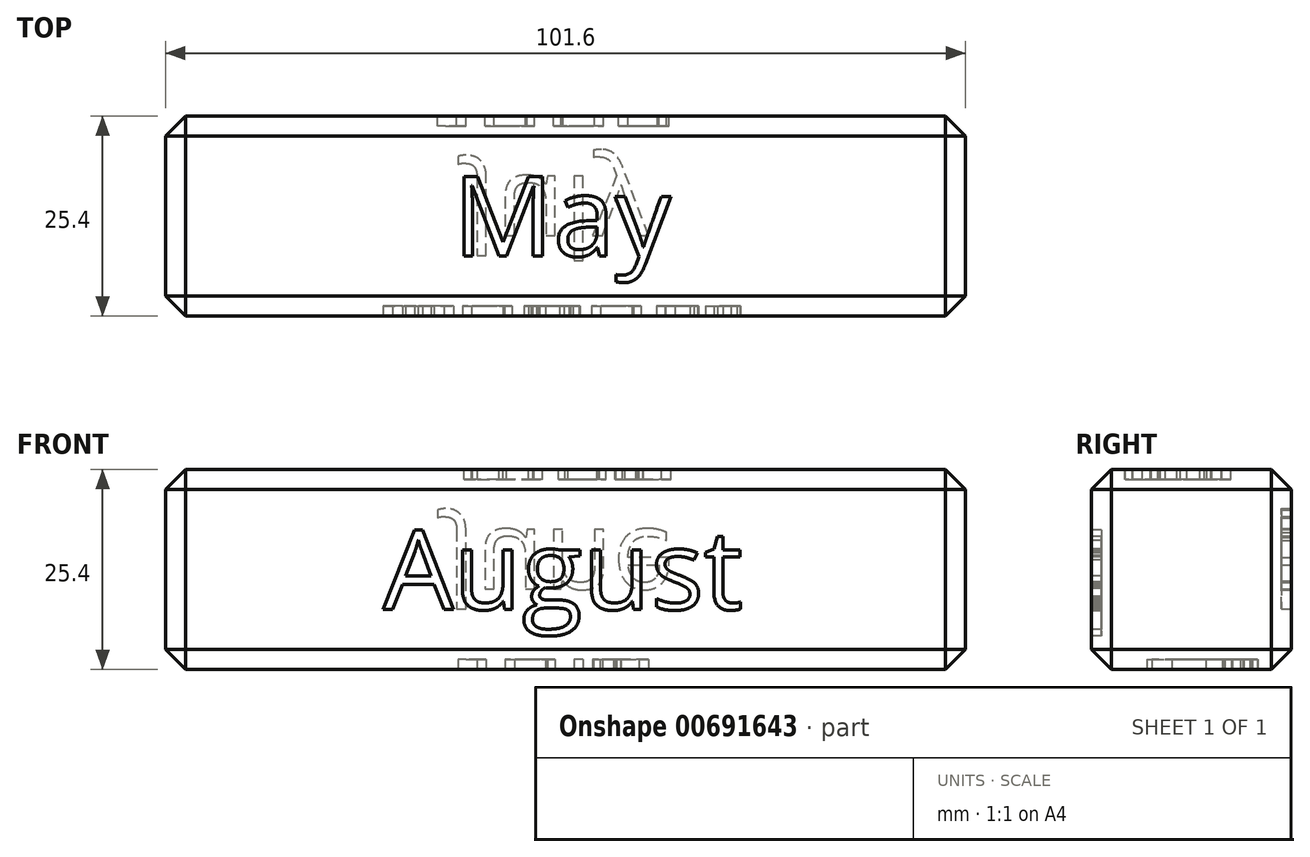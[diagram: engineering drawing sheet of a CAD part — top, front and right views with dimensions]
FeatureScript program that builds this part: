
annotation { "Feature Type Name" : "Feature", "Feature Type Description" : "" }
export const myFeature = defineFeature(function(context is Context, id is Id, definition is map)
    precondition{}
    {
        {
            var Q0;
            Q0=qCreatedBy(makeId("Top.planeOp"),FACE);
            var sketch = newSketch(context, id + "F0", { "sketchPlane" : qUnion([Q0])});
            skLineSegment(sketch, "E0.bottom", {"start": v(50.8, 12.7) * mm, "end": v(-50.8, 12.7) * mm});
            skLineSegment(sketch, "E0.top", {"start": v(50.8, -12.7) * mm, "end": v(-50.8, -12.7) * mm});
            skLineSegment(sketch, "E0.left", {"start": v(50.8, 12.7) * mm, "end": v(50.8, -12.7) * mm});
            skLineSegment(sketch, "E0.right", {"start": v(-50.8, 12.7) * mm, "end": v(-50.8, -12.7) * mm});
            skPoint(sketch, "E0.middle", {"position": v(0, 0) * mm});
            skSolve(sketch);
        }
        {
            var Q0;
            Q0 = qSketchRegion(id + "F0", true);
            extrude(context, id + "F1", {"entities" : qUnion([Q0]), "depth" : 12.7 * mm, "offsetDistance" : 25.4 * mm, "hasSecondDirection" : true, "secondDirectionOppositeDirection" : true, "secondDirectionDepth" : 12.7 * mm});
        }
        {
            var Q0;
            Q0=makeQuery(id+"F1.opExtrude","CAP_FACE",FACE,{"disambiguationData":[OSD([sQuery(id+"F0.wireOp",EDGE,"E0.bottom"),sQuery(id+"F0.wireOp",EDGE,"E0.top"),sQuery(id+"F0.wireOp",EDGE,"E0.left"),sQuery(id+"F0.wireOp",EDGE,"E0.right")])],"isStart":false});
            var Q1;
            Q1=makeQuery(id+"F1.opExtrude","SWEPT_FACE",FACE,{"disambiguationData":[OSD([sQuery(id+"F0.wireOp",EDGE,"E0.top")])]});
            var Q2;
            Q2=makeQuery(id+"F1.opExtrude","SWEPT_FACE",FACE,{"disambiguationData":[OSD([sQuery(id+"F0.wireOp",EDGE,"E0.right")])]});
            var Q3;
            Q3=makeQuery(id+"F1.opExtrude","CAP_FACE",FACE,{"disambiguationData":[OSD([sQuery(id+"F0.wireOp",EDGE,"E0.bottom"),sQuery(id+"F0.wireOp",EDGE,"E0.top"),sQuery(id+"F0.wireOp",EDGE,"E0.left"),sQuery(id+"F0.wireOp",EDGE,"E0.right")])],"isStart":true});
            var Q4;
            Q4=makeQuery(id+"F1.opExtrude","SWEPT_FACE",FACE,{"disambiguationData":[OSD([sQuery(id+"F0.wireOp",EDGE,"E0.bottom")])]});
            chamfer(context, id + "F2", {"entities" : qUnion([Q0, Q1, Q2, Q3, Q4]), "width" : 2.54 * mm, "tangentPropagation" : true});
        }
        {
            var Q0;
            Q0=makeQuery(id+"F1.opExtrude","CAP_FACE",FACE,{"disambiguationData":[OSD([sQuery(id+"F0.wireOp",EDGE,"E0.bottom"),sQuery(id+"F0.wireOp",EDGE,"E0.top"),sQuery(id+"F0.wireOp",EDGE,"E0.left"),sQuery(id+"F0.wireOp",EDGE,"E0.right")])],"isStart":false});
            var sketch = newSketch(context, id + "F3", { "sketchPlane" : qUnion([Q0])});
            skText(sketch, "E1", { "text": "May", "fontName": "OpenSans-Regular.ttf"});
            skLineSegment(sketch, "E2", {"start": v(-14.3, 0) * mm, "end": v(-61.84, 0) * mm, "construction": true});
            const initialGuessF3  = {"E1": [-0.0143, -0.00508, 1, 0, 0.01016]};
            skSetInitialGuess(sketch, initialGuessF3);
            skSolve(sketch);
        }
        {
            var Q0;
            Q0 = qSketchRegion(id + "F3", true);
            extrude(context, id + "F4", {"entities" : qUnion([Q0]), "operationType" : NewBodyOperationType.REMOVE, "oppositeDirection" : true, "depth" : 1.27 * mm, "offsetDistance" : 25.4 * mm});
        }
        {
            var Q0;
            Q0=makeQuery(id+"F1.opExtrude","SWEPT_FACE",FACE,{"disambiguationData":[OSD([sQuery(id+"F0.wireOp",EDGE,"E0.bottom")])]});
            var sketch = newSketch(context, id + "F5", { "sketchPlane" : qUnion([Q0])});
            skText(sketch, "E3", { "text": "June", "fontName": "OpenSans-Regular.ttf"});
            skLineSegment(sketch, "E4", {"start": v(58.9, 0) * mm, "end": v(15.14, 0) * mm, "construction": true});
            const initialGuessF5  = {"E3": [0.01514, 0.00508, -1, 0, 0.01016]};
            skSetInitialGuess(sketch, initialGuessF5);
            skSolve(sketch);
        }
        {
            var Q0;
            Q0 = qSketchRegion(id + "F5", true);
            extrude(context, id + "F6", {"entities" : qUnion([Q0]), "operationType" : NewBodyOperationType.REMOVE, "oppositeDirection" : true, "depth" : 1.27 * mm, "offsetDistance" : 25.4 * mm});
        }
        {
            var Q0;
            Q0=makeQuery(id+"F1.opExtrude","CAP_FACE",FACE,{"disambiguationData":[OSD([sQuery(id+"F0.wireOp",EDGE,"E0.bottom"),sQuery(id+"F0.wireOp",EDGE,"E0.top"),sQuery(id+"F0.wireOp",EDGE,"E0.left"),sQuery(id+"F0.wireOp",EDGE,"E0.right")])],"isStart":true});
            var sketch = newSketch(context, id + "F7", { "sketchPlane" : qUnion([Q0])});
            skText(sketch, "E5", { "text": "July", "fontName": "OpenSans-Regular.ttf"});
            skLineSegment(sketch, "E6", {"start": v(-57.55, 0) * mm, "end": v(-12.56, 0) * mm, "construction": true});
            const initialGuessF7  = {"E5": [-0.01256, -0.00508, 1, 0, 0.01016]};
            skSetInitialGuess(sketch, initialGuessF7);
            skSolve(sketch);
        }
        {
            var Q0;
            Q0 = qSketchRegion(id + "F7", true);
            extrude(context, id + "F8", {"entities" : qUnion([Q0]), "operationType" : NewBodyOperationType.REMOVE, "oppositeDirection" : true, "depth" : 1.27 * mm, "offsetDistance" : 25.4 * mm});
        }
        {
            var Q0;
            Q0=makeQuery(id+"F1.opExtrude","SWEPT_FACE",FACE,{"disambiguationData":[OSD([sQuery(id+"F0.wireOp",EDGE,"E0.top")])]});
            var sketch = newSketch(context, id + "F9", { "sketchPlane" : qUnion([Q0])});
            skText(sketch, "E7", { "text": "August", "fontName": "OpenSans-Regular.ttf"});
            skLineSegment(sketch, "E8", {"start": v(-61.98, 0) * mm, "end": v(-23.16, 0) * mm, "construction": true});
            const initialGuessF9  = {"E7": [-0.02316, -0.00508, 1, 0, 0.01016]};
            skSetInitialGuess(sketch, initialGuessF9);
            skSolve(sketch);
        }
        {
            var Q0;
            Q0 = qSketchRegion(id + "F9", true);
            extrude(context, id + "F10", {"entities" : qUnion([Q0]), "operationType" : NewBodyOperationType.REMOVE, "oppositeDirection" : true, "depth" : 1.27 * mm, "offsetDistance" : 25.4 * mm});
        }
    });
